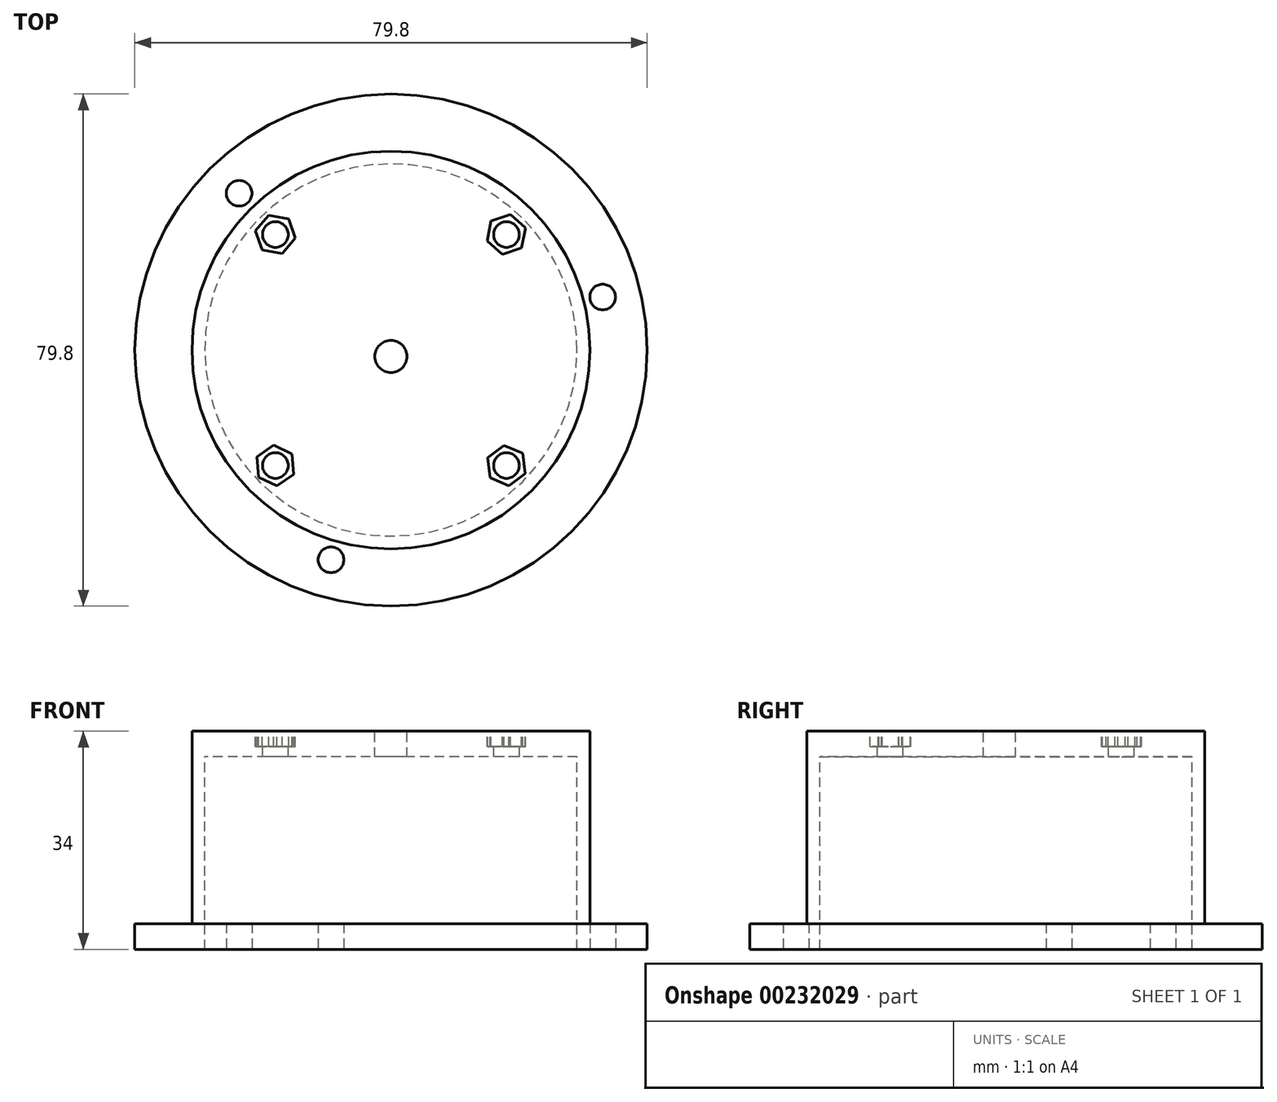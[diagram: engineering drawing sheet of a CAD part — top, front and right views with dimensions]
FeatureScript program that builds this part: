
annotation { "Feature Type Name" : "Feature", "Feature Type Description" : "" }
export const myFeature = defineFeature(function(context is Context, id is Id, definition is map)
    precondition{}
    {
        {
            var Q0;
            Q0=qCreatedBy(makeId("Top.planeOp"),FACE);
            var sketch = newSketch(context, id + "F0", { "sketchPlane" : qUnion([Q0])});
            skCircle(sketch, "E0", {"center": v(0, 0) * mm, "radius": 39.9 * mm});
            skSolve(sketch);
        }
        {
            var Q0;
            Q0 = qSketchRegion(id + "F0", true);
            extrude(context, id + "F1", {"entities" : qUnion([Q0]), "depth" : 4 * mm});
        }
        {
            var Q0;
            Q0=makeQuery(id+"F1.opExtrude","CAP_FACE",FACE,{"disambiguationData":[OSD([sQuery(id+"F0.wireOp",EDGE,"E0")])],"isStart":false});
            var sketch = newSketch(context, id + "F2", { "sketchPlane" : qUnion([Q0])});
            skCircle(sketch, "E1", {"center": v(0, 0) * mm, "radius": 29 * mm});
            skSolve(sketch);
        }
        {
            var Q0;
            Q0 = qSketchRegion(id + "F2", true);
            extrude(context, id + "F3", {"entities" : qUnion([Q0]), "operationType" : NewBodyOperationType.REMOVE, "oppositeDirection" : true, "depth" : 4 * mm});
        }
        {
            var Q0;
            Q0=makeQuery(id+"F1.opExtrude","CAP_FACE",FACE,{"disambiguationData":[OSD([sQuery(id+"F0.wireOp",EDGE,"E0")])],"isStart":false});
            var sketch = newSketch(context, id + "F4", { "sketchPlane" : qUnion([Q0])});
            skCircle(sketch, "E2", {"center": v(0, 0) * mm, "radius": 31 * mm});
            skSolve(sketch);
        }
        {
            var Q0;
            Q0 = qSketchRegion(id + "F4", true);
            extrude(context, id + "F5", {"entities" : qUnion([Q0]), "operationType" : NewBodyOperationType.ADD, "depth" : 30 * mm});
        }
        {
            var Q0;
            Q0=makeQuery(id+"F5.opExtrude","CAP_FACE",FACE,{"disambiguationData":[OSD([sQuery(id+"F4.wireOp",EDGE,"E2")])],"isStart":true});
            extrude(context, id + "F6", {"entities" : qUnion([Q0]), "operationType" : NewBodyOperationType.REMOVE, "oppositeDirection" : true, "depth" : 26 * mm});
        }
        {
            var Q0;
            Q0=makeQuery(id+"F1.opExtrude","CAP_FACE",FACE,{"disambiguationData":[OSD([sQuery(id+"F0.wireOp",EDGE,"E0")])],"isStart":true});
            var sketch = newSketch(context, id + "F7", { "sketchPlane" : qUnion([Q0])});
            skLineSegment(sketch, "E3", {"start": v(0, 0) * mm, "end": v(38.7, -9.7) * mm});
            skLineSegment(sketch, "E4", {"start": v(0, 0) * mm, "end": v(-10.96, 38.37) * mm});
            skLineSegment(sketch, "E5", {"start": v(0, 0) * mm, "end": v(-27.75, -28.67) * mm});
            skSolve(sketch);
        }
        {
            var Q0;
            {var subQ0=sQuery(id+"F7.wireOp",EDGE,"E3");var subQ1=makeQuery(id+"F1.opExtrude","CAP_EDGE",EDGE,{"disambiguationData":[OSD([sQuery(id+"F0.wireOp",EDGE,"E0")])],"isStart":true});var subQ2=makeQuery(id+"F7.imprint","INTERSECT",VERTEX,{"derivedFrom":[subQ1,subQ0]});Q0=makeQuery(id+"F7.imprint","IMPRINT",FACE,{"disambiguationData":[TD([[makeQuery(id+"F7.imprint","IMPRINT",EDGE,{"disambiguationData":[TD([[subQ2,1.0]])],"derivedFrom":subQ0}),-1.0]])]});}
            var sketch = newSketch(context, id + "F8", { "sketchPlane" : qUnion([Q0])});
            skCircle(sketch, "E6", {"center": v(-23.65, -24.43) * mm, "radius": 2 * mm});
            skCircle(sketch, "E7", {"center": v(-9.34, 32.7) * mm, "radius": 2 * mm});
            skCircle(sketch, "E8", {"center": v(32.98, -8.26) * mm, "radius": 2 * mm});
            skSolve(sketch);
        }
        {
            var Q0;
            Q0 = qSketchRegion(id + "F8", true);
            extrude(context, id + "F9", {"entities" : qUnion([Q0]), "operationType" : NewBodyOperationType.REMOVE, "oppositeDirection" : true, "depth" : 4 * mm});
        }
        {
            var Q0;
            Q0=makeQuery(id+"F5.opExtrude","CAP_FACE",FACE,{"disambiguationData":[OSD([sQuery(id+"F4.wireOp",EDGE,"E2")])],"isStart":false});
            var sketch = newSketch(context, id + "F10", { "sketchPlane" : qUnion([Q0])});
            skLineSegment(sketch, "E9.bottom", {"start": v(18, 18) * mm, "end": v(-18, 18) * mm});
            skLineSegment(sketch, "E9.top", {"start": v(18, -18) * mm, "end": v(-18, -18) * mm});
            skLineSegment(sketch, "E9.left", {"start": v(18, 18) * mm, "end": v(18, -18) * mm});
            skLineSegment(sketch, "E9.right", {"start": v(-18, 18) * mm, "end": v(-18, -18) * mm});
            skSolve(sketch);
        }
        {
            var Q0;
            Q0=makeQuery(id+"F10.imprint","IMPRINT",FACE,{"disambiguationData":[TD([[makeQuery(id+"F10.imprint","IMPRINT",EDGE,{"derivedFrom":sQuery(id+"F10.wireOp",EDGE,"E9.bottom")}),1.0]])]});
            var sketch = newSketch(context, id + "F11", { "sketchPlane" : qUnion([Q0])});
            skCircle(sketch, "E10", {"center": v(18, 18) * mm, "radius": 2 * mm});
            skCircle(sketch, "E11", {"center": v(-18, 18) * mm, "radius": 2 * mm});
            skCircle(sketch, "E12", {"center": v(-18, -18) * mm, "radius": 2 * mm});
            skCircle(sketch, "E13", {"center": v(18, -18) * mm, "radius": 2 * mm});
            skSolve(sketch);
        }
        {
            var Q0;
            Q0 = qSketchRegion(id + "F11", true);
            extrude(context, id + "F12", {"entities" : qUnion([Q0]), "operationType" : NewBodyOperationType.REMOVE, "oppositeDirection" : true, "depth" : 4 * mm});
        }
        {
            var Q0;
            Q0=makeQuery(id+"F10.imprint","IMPRINT",FACE,{"disambiguationData":[TD([[makeQuery(id+"F10.imprint","IMPRINT",EDGE,{"derivedFrom":sQuery(id+"F10.wireOp",EDGE,"E9.bottom")}),1.0]])]});
            var sketch = newSketch(context, id + "F13", { "sketchPlane" : qUnion([Q0])});
            skCircle(sketch, "E14", {"center": v(0, -1) * mm, "radius": 2.5 * mm});
            skSolve(sketch);
        }
        {
            var Q0;
            Q0 = qSketchRegion(id + "F13", true);
            extrude(context, id + "F14", {"entities" : qUnion([Q0]), "operationType" : NewBodyOperationType.REMOVE, "oppositeDirection" : true, "depth" : 4 * mm});
        }
        {
            var Q0;
            Q0=makeQuery(id+"F10.imprint","IMPRINT",FACE,{"disambiguationData":[TD([[makeQuery(id+"F10.imprint","IMPRINT",EDGE,{"derivedFrom":sQuery(id+"F10.wireOp",EDGE,"E9.bottom")}),-1.0]])]});
            var sketch = newSketch(context, id + "F15", { "sketchPlane" : qUnion([Q0])});
            skCircle(sketch, "E15.cCircle", {"center": v(18, -18) * mm, "radius": 3.18 * mm, "construction": true});
            skLineSegment(sketch, "E15.0", {"start": v(18.38, -21.15) * mm, "end": v(15.46, -19.9) * mm});
            skLineSegment(sketch, "E15.1", {"start": v(15.46, -19.9) * mm, "end": v(15.08, -16.75) * mm});
            skLineSegment(sketch, "E15.2", {"start": v(15.08, -16.75) * mm, "end": v(17.62, -14.85) * mm});
            skLineSegment(sketch, "E15.3", {"start": v(17.62, -14.85) * mm, "end": v(20.54, -16.1) * mm});
            skLineSegment(sketch, "E15.4", {"start": v(20.54, -16.1) * mm, "end": v(20.92, -19.25) * mm});
            skLineSegment(sketch, "E15.5", {"start": v(20.92, -19.25) * mm, "end": v(18.38, -21.15) * mm});
            skCircle(sketch, "E16.cCircle", {"center": v(-18, -18) * mm, "radius": 3.18 * mm, "construction": true});
            skLineSegment(sketch, "E16.0", {"start": v(-17.75, -21.17) * mm, "end": v(-20.62, -19.8) * mm});
            skLineSegment(sketch, "E16.1", {"start": v(-20.62, -19.8) * mm, "end": v(-20.87, -16.64) * mm});
            skLineSegment(sketch, "E16.2", {"start": v(-20.87, -16.64) * mm, "end": v(-18.25, -14.83) * mm});
            skLineSegment(sketch, "E16.3", {"start": v(-18.25, -14.83) * mm, "end": v(-15.38, -16.2) * mm});
            skLineSegment(sketch, "E16.4", {"start": v(-15.38, -16.2) * mm, "end": v(-15.13, -19.36) * mm});
            skLineSegment(sketch, "E16.5", {"start": v(-15.13, -19.36) * mm, "end": v(-17.75, -21.17) * mm});
            skCircle(sketch, "E17.cCircle", {"center": v(17.99, 18) * mm, "radius": 3.18 * mm, "construction": true});
            skLineSegment(sketch, "E17.0", {"start": v(17.35, 14.89) * mm, "end": v(14.98, 17) * mm});
            skLineSegment(sketch, "E17.1", {"start": v(14.98, 17) * mm, "end": v(15.61, 20.1) * mm});
            skLineSegment(sketch, "E17.2", {"start": v(15.61, 20.1) * mm, "end": v(18.62, 21.11) * mm});
            skLineSegment(sketch, "E17.3", {"start": v(18.62, 21.11) * mm, "end": v(21, 19) * mm});
            skLineSegment(sketch, "E17.4", {"start": v(21, 19) * mm, "end": v(20.36, 15.9) * mm});
            skLineSegment(sketch, "E17.5", {"start": v(20.36, 15.9) * mm, "end": v(17.35, 14.89) * mm});
            skCircle(sketch, "E18.cCircle", {"center": v(-18, 18) * mm, "radius": 3.18 * mm, "construction": true});
            skLineSegment(sketch, "E18.0", {"start": v(-16.94, 15) * mm, "end": v(-20.07, 15.59) * mm});
            skLineSegment(sketch, "E18.1", {"start": v(-20.07, 15.59) * mm, "end": v(-21.12, 18.58) * mm});
            skLineSegment(sketch, "E18.2", {"start": v(-21.12, 18.58) * mm, "end": v(-19.06, 21) * mm});
            skLineSegment(sketch, "E18.3", {"start": v(-19.06, 21) * mm, "end": v(-15.93, 20.41) * mm});
            skLineSegment(sketch, "E18.4", {"start": v(-15.93, 20.41) * mm, "end": v(-14.88, 17.42) * mm});
            skLineSegment(sketch, "E18.5", {"start": v(-14.88, 17.42) * mm, "end": v(-16.94, 15) * mm});
            skSolve(sketch);
        }
        {
            var Q0;
            Q0 = qSketchRegion(id + "F15", true);
            extrude(context, id + "F16", {"entities" : qUnion([Q0]), "operationType" : NewBodyOperationType.REMOVE, "oppositeDirection" : true, "depth" : 2.4 * mm});
        }
    });
